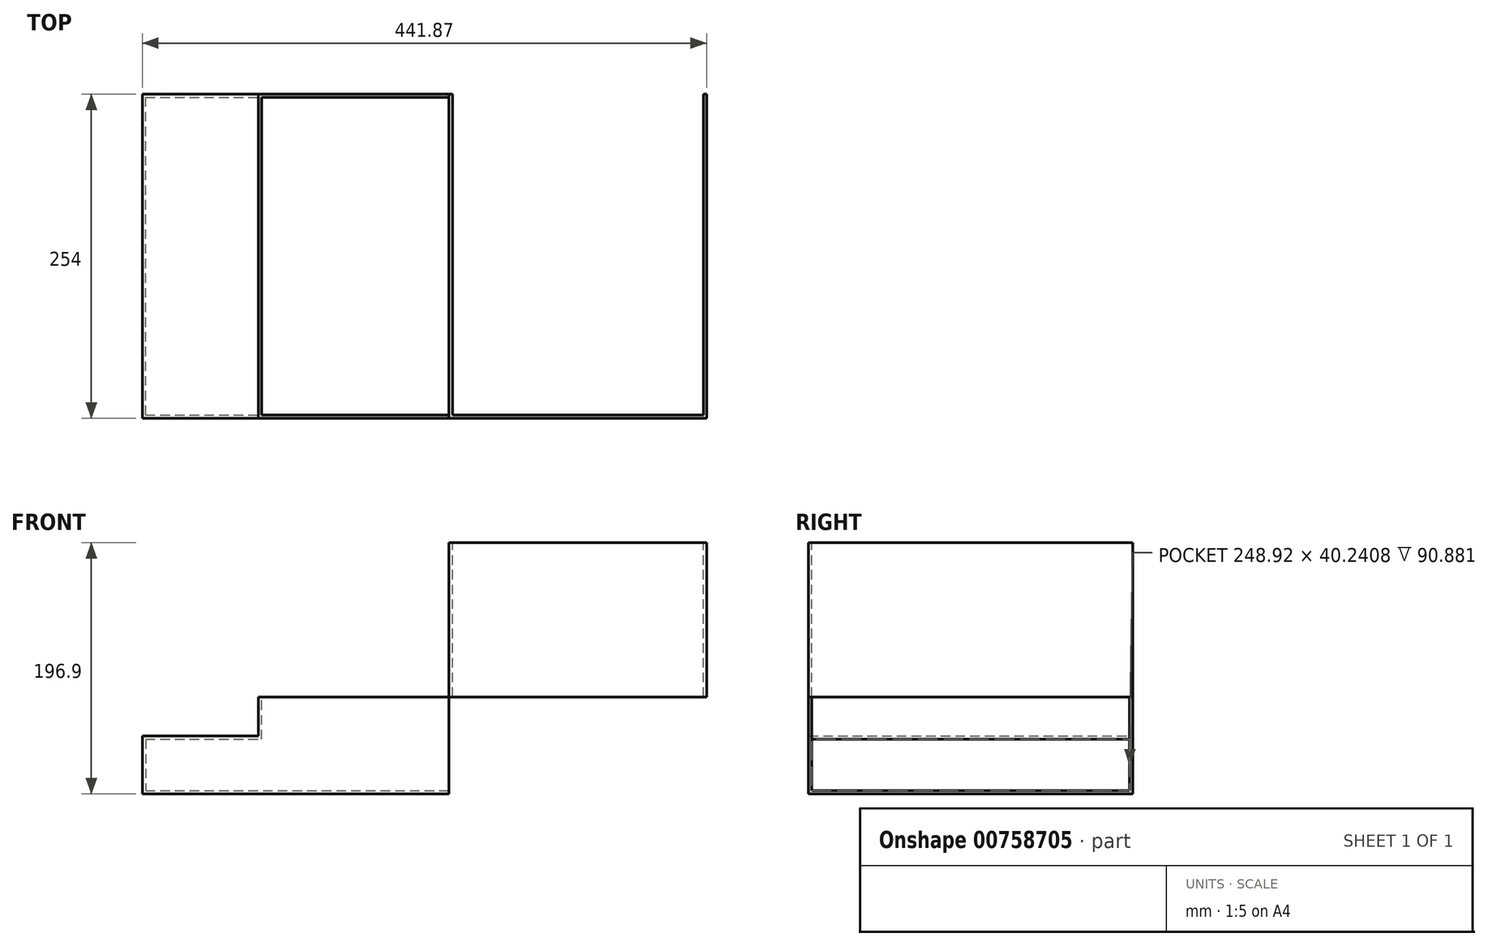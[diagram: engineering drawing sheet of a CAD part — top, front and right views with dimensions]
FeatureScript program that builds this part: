
annotation { "Feature Type Name" : "Feature", "Feature Type Description" : "" }
export const myFeature = defineFeature(function(context is Context, id is Id, definition is map)
    precondition{}
    {
        {
            var Q0;
            Q0=qCreatedBy(makeId("Front.planeOp"),FACE);
            var sketch = newSketch(context, id + "F0", { "sketchPlane" : qUnion([Q0])});
            skLineSegment(sketch, "E0.bottom", {"start": v(-248.36, -68.3) * mm, "end": v(-157.48, -68.3) * mm});
            skLineSegment(sketch, "E0.top", {"start": v(-248.36, -113.62) * mm, "end": v(-157.48, -113.62) * mm});
            skLineSegment(sketch, "E0.left", {"start": v(-248.36, -68.3) * mm, "end": v(-248.36, -113.62) * mm});
            skLineSegment(sketch, "E0.right", {"start": v(-157.48, -68.3) * mm, "end": v(-157.48, -113.62) * mm});
            skLineSegment(sketch, "E1.bottom", {"start": v(-157.48, -113.62) * mm, "end": v(-8.1, -113.62) * mm});
            skLineSegment(sketch, "E1.top", {"start": v(-157.48, -37.6) * mm, "end": v(-8.1, -37.6) * mm});
            skLineSegment(sketch, "E1.left", {"start": v(-157.48, -113.62) * mm, "end": v(-157.48, -37.6) * mm});
            skLineSegment(sketch, "E1.right", {"start": v(-8.1, -113.62) * mm, "end": v(-8.1, -37.6) * mm});
            skLineSegment(sketch, "E2.bottom", {"start": v(-8.1, -37.6) * mm, "end": v(193.51, -37.6) * mm});
            skLineSegment(sketch, "E2.top", {"start": v(-8.1, 83.28) * mm, "end": v(193.51, 83.28) * mm});
            skLineSegment(sketch, "E2.left", {"start": v(-8.1, -37.6) * mm, "end": v(-8.1, 83.28) * mm});
            skLineSegment(sketch, "E2.right", {"start": v(193.51, -37.6) * mm, "end": v(193.51, 83.28) * mm});
            skSolve(sketch);
        }
        {
            var Q0;
            Q0 = qSketchRegion(id + "F0", true);
            extrude(context, id + "F1", {"entities" : qUnion([Q0]), "depth" : 254 * mm, "offsetDistance" : 25.4 * mm});
        }
        {
            var Q0;
            Q0=makeQuery(id+"F1.opExtrude","SWEPT_FACE",FACE,{"disambiguationData":[OSD([sQuery(id+"F0.wireOp",EDGE,"E2.top")])]});
            var Q1;
            Q1=makeQuery(id+"F1.opExtrude","SWEPT_FACE",FACE,{"disambiguationData":[OSD([sQuery(id+"F0.wireOp",EDGE,"E1.top")])]});
            var Q2;
            Q2=makeQuery(id+"F1.opExtrude","SWEPT_FACE",FACE,{"disambiguationData":[OSD([sQuery(id+"F0.wireOp",EDGE,"E2.bottom")])]});
            var Q3;
            Q3=makeQuery(id+"F1.opExtrude","SWEPT_FACE",FACE,{"disambiguationData":[OSD([sQuery(id+"F0.wireOp",EDGE,"E1.right")])]});
            var Q4;
            Q4=makeQuery(id+"F1.opExtrude","CAP_FACE",FACE,{"disambiguationData":[OSD([sQuery(id+"F0.wireOp",EDGE,"E2.bottom"),sQuery(id+"F0.wireOp",EDGE,"E2.top"),sQuery(id+"F0.wireOp",EDGE,"E2.left"),sQuery(id+"F0.wireOp",EDGE,"E2.right")])],"isStart":true});
            shell(context, id + "F2", {"entities" : qUnion([Q0, Q1, Q2, Q3, Q4]), "thickness" : 2.54 * mm});
        }
    });
